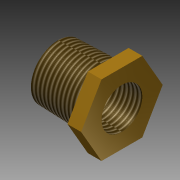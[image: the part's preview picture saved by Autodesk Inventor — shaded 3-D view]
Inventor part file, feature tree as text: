
AUTODESK INVENTOR PART (.ipt)
format: ipt  version: 2011 (Build 150239000, 239)  size: 104,448 bytes
history: native  units: mm (DEFAULTED — no unit token found)
features: thread x4, sketch x1, imported_body x1
ambient origin geometry x8: Origin, YZ Plane, XZ Plane, XY Plane, X Axis, Y Axis, Z Axis, Center Point
bodies: Solid1 (feature_tree)
feature tree (6):
  sketch  "Sketch1"
  imported_body  "Base1"
  thread  "Thread1"  [1 undecoded]
  thread  "Thread2"  [1 undecoded]
  thread  "Thread3"  [1 undecoded]
  thread  "Thread4"  [1 undecoded]
note: 4 required parameter values undecoded (feature->parameter linkage not recoverable at this tier; creation-order binding heuristic only, values carry confidence <= 0.55)
